# Revit family: Lighting_Round_LED_StarTek_Halo-Direct1
name_source: partatom
category: Lighting Fixtures
units: mm (PartAtom-declared; Revit-internal decimal feet)

## family parameters
Cut with Voids When Loaded = No
Host = Face
Light Source = Yes
OmniClass Number = 23.80.70.11
OmniClass Title = Luminaries for Internal Lighting
Part Type = Normal
Room Calculation Point = No
Round Connector Dimension = Use Diameter
Shared = No

## types (1)
- Default - please load Revit Family Type Catalog
    ****Power Options = This fixture has direct fixture power or remote power.  PCX - Powered Canopy. RSMX - Remote Surface Mount or RIWX - Remote in Wall. Available in White (W) or Black (B).
    2' Fixtures = No
    3' Fixtures = No
    4' Fixtures = Yes
    Apparent Load = 26 VA
    Assembly Code = D5020200
    CRI = 80
    Color Filter = 16777215
    Default Elevation = 4' - 0"
    Description = Halo Direct
    Diameter = 4' - 0"
    Dimming Lamp Color Temperature Shift = <None>
    Distribution = SD - SatinIce Diffuse
    Emit Shape Visible in Rendering = No
    Emit from Circle Diameter = 4' - 0"
    Frequency = 60 Hz
    Height = 0' - 1 1/2"
    Input Wattage = 24 W
    Keynote = 16500
    Lamp = LED
    Manufacturer = StarTek Lighting
    Number of Poles = 1
    Output = High
    Phase = 1
    Photometric Note = Import IES files https://starteklightingamerica.com
    Photometric Web File = Generic Light Source Shown : Please download and link the IES file that best matches your fixture specification
    Power Factor = 0.93
    Product data url = https://bimobject.com
    Tilt Angle = 90.00°
    URL = https://starteklightingamerica.com
    Voltage = 120 V
    Voltage Range = 120-277V
    Wattage Comments = Efficacy up to 120 lm/W
    Weight = 0.00 lbf

## geometry (parser evidence)
native form markers: Sweep x9
no freeform markers — native parametric forms only
